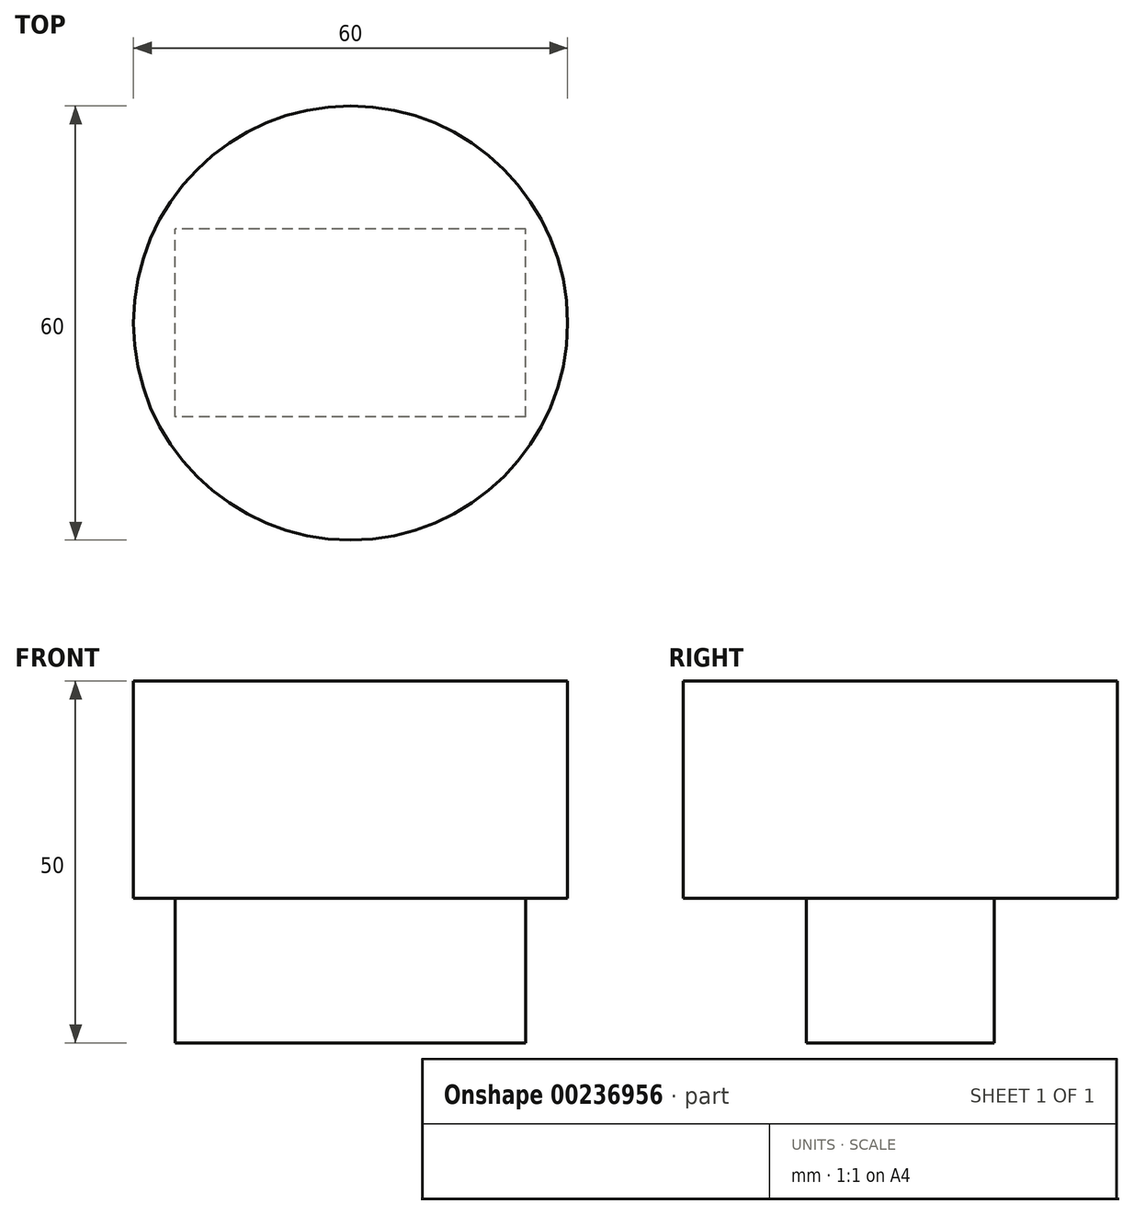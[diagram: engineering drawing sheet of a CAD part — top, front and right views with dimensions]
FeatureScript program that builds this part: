
annotation { "Feature Type Name" : "Feature", "Feature Type Description" : "" }
export const myFeature = defineFeature(function(context is Context, id is Id, definition is map)
    precondition{}
    {
        {
            var Q0;
            Q0=qCreatedBy(makeId("Top.planeOp"),FACE);
            var sketch = newSketch(context, id + "F0", { "sketchPlane" : qUnion([Q0])});
            skLineSegment(sketch, "E0.bottom", {"start": v(24.23, -13) * mm, "end": v(-24.23, -13) * mm});
            skLineSegment(sketch, "E0.top", {"start": v(24.23, 13) * mm, "end": v(-24.23, 13) * mm});
            skLineSegment(sketch, "E0.left", {"start": v(24.23, -13) * mm, "end": v(24.23, 13) * mm});
            skLineSegment(sketch, "E0.right", {"start": v(-24.23, -13) * mm, "end": v(-24.23, 13) * mm});
            skPoint(sketch, "E0.middle", {"position": v(0, 0) * mm});
            skCircle(sketch, "E1", {"center": v(0, 0) * mm, "radius": 27.5 * mm});
            skSolve(sketch);
        }
        {
            var Q0;
            Q0=makeQuery(id+"F0.imprint","IMPRINT",FACE,{"disambiguationData":[TD([[makeQuery(id+"F0.imprint","IMPRINT",EDGE,{"derivedFrom":sQuery(id+"F0.wireOp",EDGE,"E0.bottom")}),-1.0]])]});
            extrude(context, id + "F1", {"entities" : qUnion([Q0]), "depth" : 20 * mm});
        }
        {
            var Q0;
            Q0=makeQuery(id+"F1.opExtrude","CAP_FACE",FACE,{"disambiguationData":[OSD([sQuery(id+"F0.wireOp",EDGE,"E0.bottom"),sQuery(id+"F0.wireOp",EDGE,"E0.top"),sQuery(id+"F0.wireOp",EDGE,"E0.left"),sQuery(id+"F0.wireOp",EDGE,"E0.right")])],"isStart":false});
            cPlane(context, id + "F2", {"entities" : qUnion([Q0]), "cplaneType" : CPlaneType.OFFSET, "offset" : 20 * mm, "width" : 150 * mm, "height" : 150 * mm});
        }
        {
            var Q0;
            Q0=qCreatedBy(id+"F2.planeOp",FACE);
            var sketch = newSketch(context, id + "F3", { "sketchPlane" : qUnion([Q0])});
            skCircle(sketch, "E2", {"center": v(0, 0) * mm, "radius": 30 * mm});
            skSolve(sketch);
        }
        {
            var Q0;
            Q0=makeQuery(id+"F1.opExtrude","CAP_FACE",FACE,{"disambiguationData":[OSD([sQuery(id+"F0.wireOp",EDGE,"E0.bottom"),sQuery(id+"F0.wireOp",EDGE,"E0.top"),sQuery(id+"F0.wireOp",EDGE,"E0.left"),sQuery(id+"F0.wireOp",EDGE,"E0.right")])],"isStart":false});
            var sketch = newSketch(context, id + "F4", { "sketchPlane" : qUnion([Q0])});
            skCircle(sketch, "E3", {"center": v(0, 0) * mm, "radius": 30 * mm});
            skSolve(sketch);
        }
        {
            var Q0;
            Q0 = qSketchRegion(id + "F4", true);
            extrude(context, id + "F5", {"entities" : qUnion([Q0]), "operationType" : NewBodyOperationType.ADD, "depth" : 30 * mm});
        }
    });
